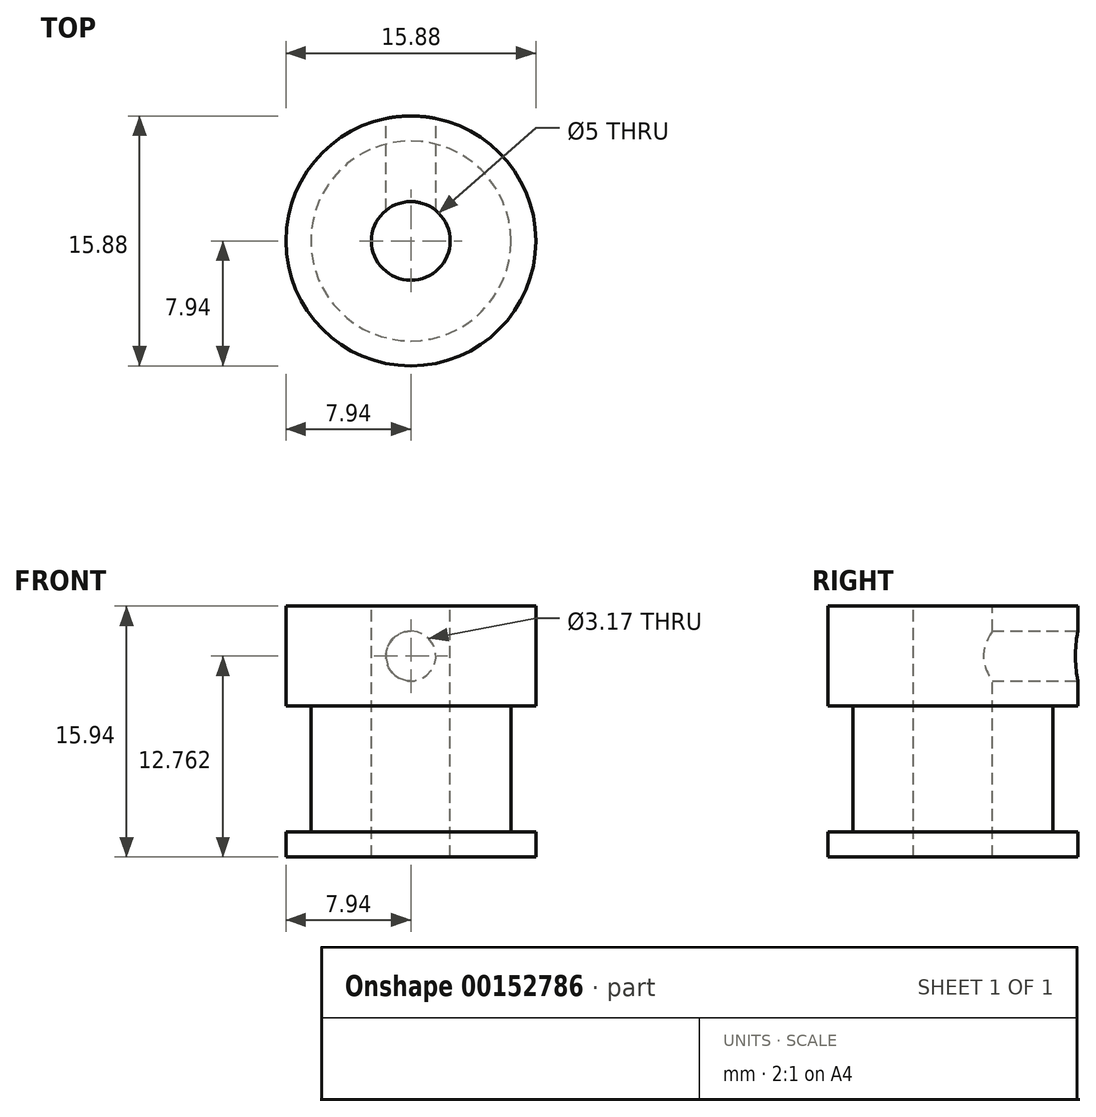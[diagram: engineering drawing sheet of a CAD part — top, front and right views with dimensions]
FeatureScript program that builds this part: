
annotation { "Feature Type Name" : "Feature", "Feature Type Description" : "" }
export const myFeature = defineFeature(function(context is Context, id is Id, definition is map)
    precondition{}
    {
        {
            var Q0;
            Q0=qCreatedBy(makeId("Top.planeOp"),FACE);
            var sketch = newSketch(context, id + "F0", { "sketchPlane" : qUnion([Q0])});
            skCircle(sketch, "E0", {"center": v(0, 0) * mm, "radius": 7.94 * mm});
            skSolve(sketch);
        }
        {
            var Q0;
            Q0 = qSketchRegion(id + "F0", true);
            extrude(context, id + "F1", {"entities" : qUnion([Q0]), "depth" : 1.59 * mm});
        }
        {
            var Q0;
            Q0=makeQuery(id+"F1.opExtrude","CAP_FACE",FACE,{"disambiguationData":[OSD([sQuery(id+"F0.wireOp",EDGE,"E0")])],"isStart":false});
            var sketch = newSketch(context, id + "F2", { "sketchPlane" : qUnion([Q0])});
            skCircle(sketch, "E1", {"center": v(0, 0) * mm, "radius": 6.35 * mm});
            skSolve(sketch);
        }
        {
            var Q0;
            Q0 = qSketchRegion(id + "F2", true);
            extrude(context, id + "F3", {"entities" : qUnion([Q0]), "operationType" : NewBodyOperationType.ADD, "depth" : 8 * mm});
        }
        {
            var Q0;
            Q0=makeQuery(id+"F3.opExtrude","CAP_FACE",FACE,{"disambiguationData":[OSD([sQuery(id+"F2.wireOp",EDGE,"E1")])],"isStart":false});
            var sketch = newSketch(context, id + "F4", { "sketchPlane" : qUnion([Q0])});
            skCircle(sketch, "E2", {"center": v(0, 0) * mm, "radius": 7.94 * mm, "construction": true});
            skLineSegment(sketch, "E3.bottom", {"start": v(7.94, -7.94) * mm, "end": v(-7.94, -7.94) * mm});
            skLineSegment(sketch, "E3.top", {"start": v(7.94, 7.94) * mm, "end": v(-7.94, 7.94) * mm});
            skLineSegment(sketch, "E3.left", {"start": v(7.94, -7.94) * mm, "end": v(7.94, 7.94) * mm});
            skLineSegment(sketch, "E3.right", {"start": v(-7.94, -7.94) * mm, "end": v(-7.94, 7.94) * mm});
            skSolve(sketch);
        }
        {
            var Q0;
            Q0 = qSketchRegion(id + "F4", true);
            extrude(context, id + "F5", {"entities" : qUnion([Q0]), "operationType" : NewBodyOperationType.ADD, "depth" : 6.35 * mm});
        }
        {
            var Q0;
            Q0=makeQuery(id+"F5.opExtrude","CAP_FACE",FACE,{"disambiguationData":[OSD([sQuery(id+"F4.wireOp",EDGE,"E3.bottom"),sQuery(id+"F4.wireOp",EDGE,"E3.top"),sQuery(id+"F4.wireOp",EDGE,"E3.left"),sQuery(id+"F4.wireOp",EDGE,"E3.right")])],"isStart":false});
            var sketch = newSketch(context, id + "F6", { "sketchPlane" : qUnion([Q0])});
            skCircle(sketch, "E4", {"center": v(0, 0) * mm, "radius": 2.5 * mm});
            skSolve(sketch);
        }
        {
            var Q0;
            Q0 = qSketchRegion(id + "F6", true);
            var Q1;
            Q1=makeQuery(id+"F1.opExtrude","CAP_FACE",FACE,{"disambiguationData":[OSD([sQuery(id+"F0.wireOp",EDGE,"E0")])],"isStart":true});
            extrude(context, id + "F7", {"entities" : qUnion([Q0]), "operationType" : NewBodyOperationType.REMOVE, "endBound" : BoundingType.UP_TO_SURFACE, "oppositeDirection" : true, "endBoundEntityFace" : qUnion([Q1]), "depth" : 25.4 * mm});
        }
        {
            var Q0;
            Q0=makeQuery(id+"F5.opExtrude","SWEPT_FACE",FACE,{"disambiguationData":[OSD([sQuery(id+"F4.wireOp",EDGE,"E3.top")])]});
            var sketch = newSketch(context, id + "F8", { "sketchPlane" : qUnion([Q0])});
            skLineSegment(sketch, "E5", {"start": v(0, 15.94) * mm, "end": v(0, 9.59) * mm, "construction": true});
            skCircle(sketch, "E6", {"center": v(0, 12.76) * mm, "radius": 1.59 * mm});
            skSolve(sketch);
        }
        {
            var Q0;
            Q0 = qSketchRegion(id + "F8", true);
            var Q1;
            Q1=makeQuery(id+"F7.boolean.opBoolean","COPY",FACE,{"derivedFrom":makeQuery(id+"F7.opExtrude","SWEPT_FACE",FACE,{"disambiguationData":[OSD([sQuery(id+"F6.wireOp",EDGE,"E4")])]})});
            extrude(context, id + "F9", {"entities" : qUnion([Q0]), "operationType" : NewBodyOperationType.REMOVE, "endBound" : BoundingType.UP_TO_SURFACE, "oppositeDirection" : true, "endBoundEntityFace" : qUnion([Q1]), "depth" : 25.4 * mm});
        }
        {
            var Q0;
            Q0=makeQuery(id+"F5.opExtrude","SWEPT_EDGE",EDGE,{"disambiguationData":[OSD([sQuery(id+"F4.wireOp",EDGE,"E3.top"),sQuery(id+"F4.wireOp",EDGE,"E3.right")])]});
            var Q1;
            Q1=makeQuery(id+"F5.opExtrude","SWEPT_EDGE",EDGE,{"disambiguationData":[OSD([sQuery(id+"F4.wireOp",EDGE,"E3.bottom"),sQuery(id+"F4.wireOp",EDGE,"E3.right")])]});
            var Q2;
            Q2=makeQuery(id+"F5.opExtrude","SWEPT_EDGE",EDGE,{"disambiguationData":[OSD([sQuery(id+"F4.wireOp",EDGE,"E3.top"),sQuery(id+"F4.wireOp",EDGE,"E3.left")])]});
            var Q3;
            Q3=makeQuery(id+"F5.opExtrude","SWEPT_EDGE",EDGE,{"disambiguationData":[OSD([sQuery(id+"F4.wireOp",EDGE,"E3.bottom"),sQuery(id+"F4.wireOp",EDGE,"E3.left")])]});
            fillet(context, id + "F10", {"entities" : qUnion([Q0, Q1, Q2, Q3]), "radius" : 7.94 * mm, "tangentPropagation" : true, "allowEdgeOverflow" : false});
        }
    });
